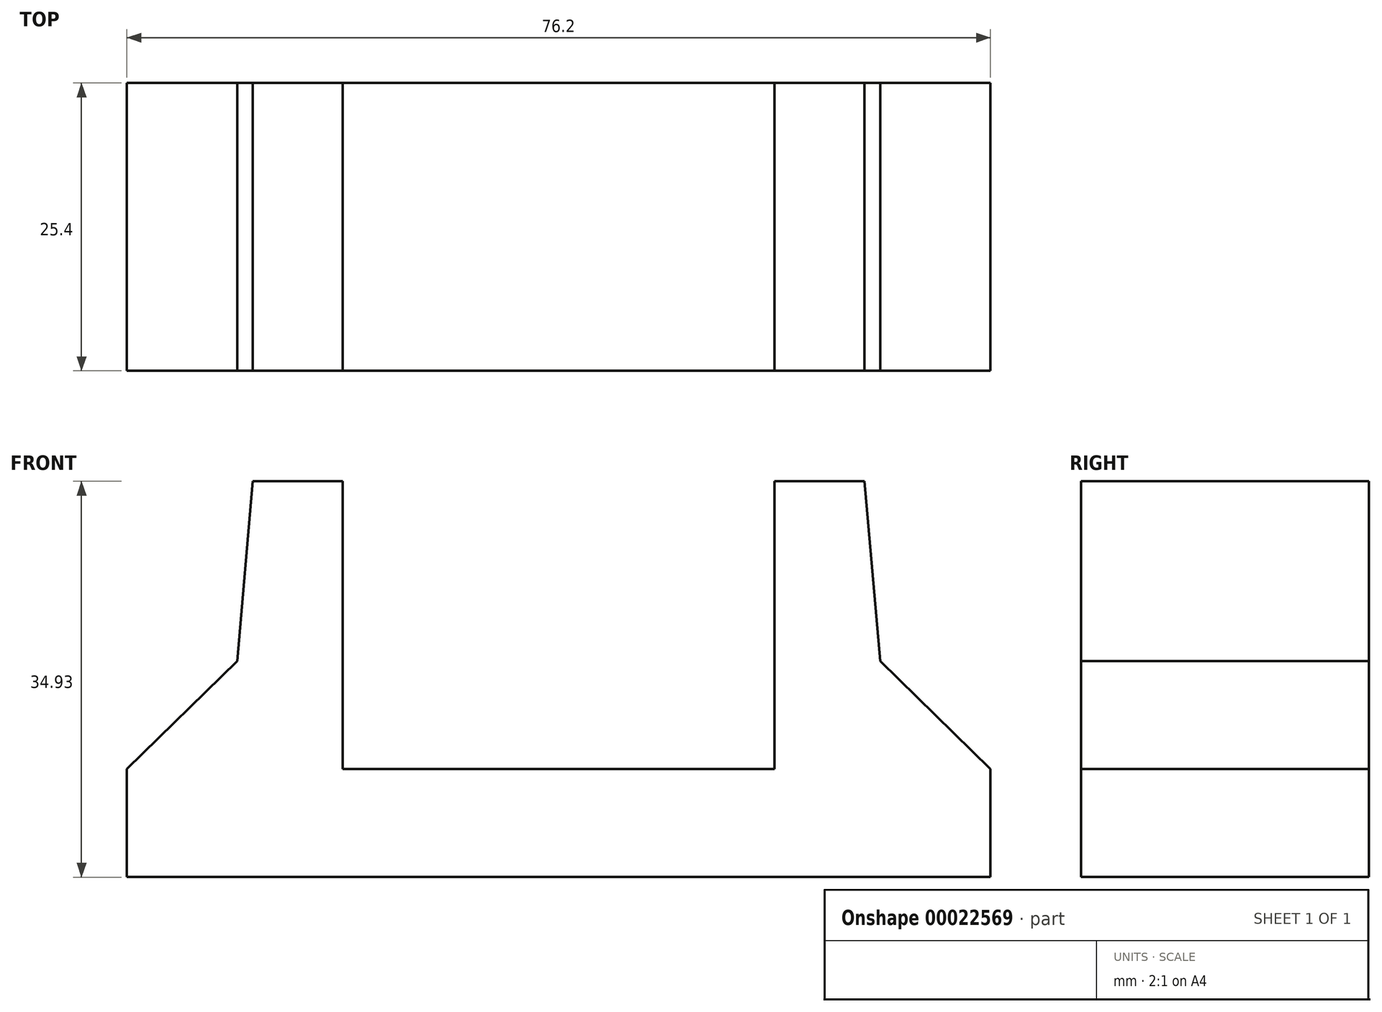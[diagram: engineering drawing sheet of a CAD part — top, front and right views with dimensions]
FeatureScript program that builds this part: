
annotation { "Feature Type Name" : "Feature", "Feature Type Description" : "" }
export const myFeature = defineFeature(function(context is Context, id is Id, definition is map)
    precondition{}
    {
        {
            var Q0;
            Q0=qCreatedBy(makeId("Front.planeOp"),FACE);
            var sketch = newSketch(context, id + "F0", { "sketchPlane" : qUnion([Q0])});
            skLineSegment(sketch, "E0", {"start": v(0, 0) * mm, "end": v(0, 81.74) * mm, "construction": true});
            skLineSegment(sketch, "E1", {"start": v(0, 0) * mm, "end": v(19.05, 0) * mm});
            skLineSegment(sketch, "E2", {"start": v(19.05, 0) * mm, "end": v(19.05, 25.4) * mm});
            skLineSegment(sketch, "E3", {"start": v(19.05, 25.4) * mm, "end": v(26.99, 25.4) * mm});
            skLineSegment(sketch, "E4", {"start": v(26.99, 25.4) * mm, "end": v(28.38, 9.53) * mm});
            skLineSegment(sketch, "E5", {"start": v(28.38, 9.53) * mm, "end": v(38.1, 0) * mm});
            skLineSegment(sketch, "E6", {"start": v(38.1, 0) * mm, "end": v(38.1, -9.52) * mm});
            skLineSegment(sketch, "E7", {"start": v(38.1, -9.52) * mm, "end": v(0, -9.53) * mm});
            skLineSegment(sketch, "E8.MirrorCS", {"start": v(0, 0) * mm, "end": v(-19.05, 0) * mm});
            skLineSegment(sketch, "E9.MirrorCS", {"start": v(-26.99, 25.4) * mm, "end": v(-28.38, 9.52) * mm});
            skLineSegment(sketch, "E10.MirrorCS", {"start": v(-28.38, 9.53) * mm, "end": v(-38.1, 0) * mm});
            skLineSegment(sketch, "E11.MirrorCS", {"start": v(-19.05, 25.4) * mm, "end": v(-26.99, 25.4) * mm});
            skLineSegment(sketch, "E12.MirrorCS", {"start": v(-38.1, -9.53) * mm, "end": v(0, -9.52) * mm});
            skLineSegment(sketch, "E13.MirrorCS", {"start": v(-19.05, 0) * mm, "end": v(-19.05, 25.4) * mm});
            skLineSegment(sketch, "E14.MirrorCS", {"start": v(-38.1, 0) * mm, "end": v(-38.1, -9.52) * mm});
            skSolve(sketch);
        }
        {
            var Q0;
            Q0 = qSketchRegion(id + "F0", true);
            extrude(context, id + "F1", {"entities" : qUnion([Q0]), "depth" : 25.4 * mm});
        }
    });
